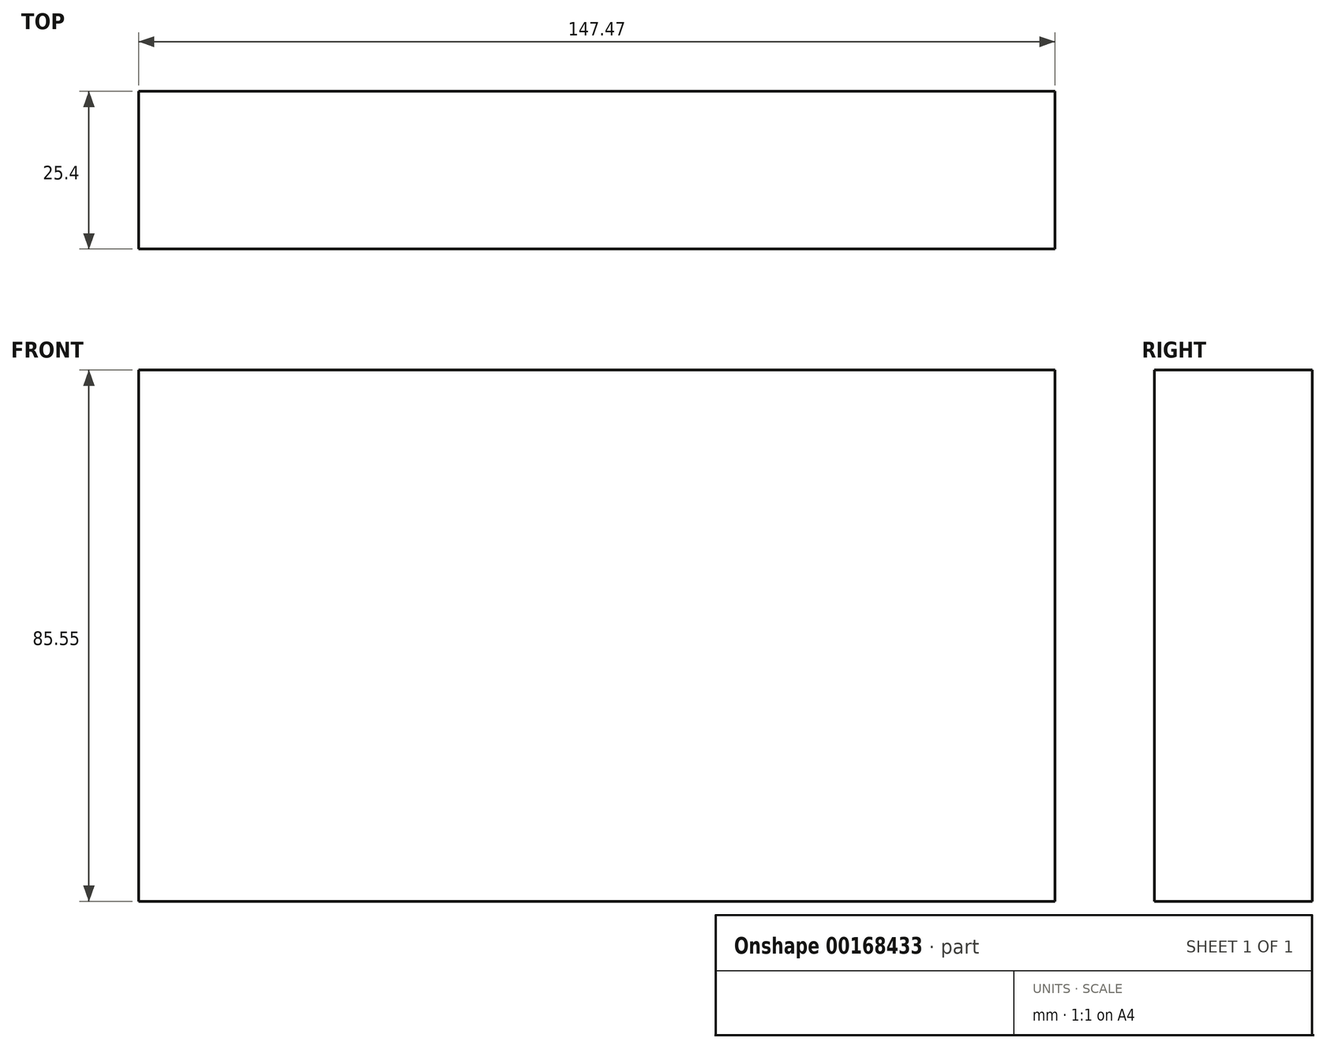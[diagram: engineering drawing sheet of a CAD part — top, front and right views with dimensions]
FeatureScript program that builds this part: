
annotation { "Feature Type Name" : "Feature", "Feature Type Description" : "" }
export const myFeature = defineFeature(function(context is Context, id is Id, definition is map)
    precondition{}
    {
        {
            var Q0;
            Q0=qCreatedBy(makeId("Front.planeOp"),FACE);
            var sketch = newSketch(context, id + "F0", { "sketchPlane" : qUnion([Q0])});
            skLineSegment(sketch, "E0.bottom", {"start": v(44.27, 43.86) * mm, "end": v(-103.2, 43.86) * mm});
            skLineSegment(sketch, "E0.top", {"start": v(44.27, 129.41) * mm, "end": v(-103.2, 129.41) * mm});
            skLineSegment(sketch, "E0.left", {"start": v(44.27, 43.86) * mm, "end": v(44.27, 129.41) * mm});
            skLineSegment(sketch, "E0.right", {"start": v(-103.2, 43.86) * mm, "end": v(-103.2, 129.41) * mm});
            skPoint(sketch, "E0.middle", {"position": v(-29.46, 86.64) * mm});
            skSolve(sketch);
        }
        {
            var Q0;
            Q0 = qSketchRegion(id + "F0", true);
            extrude(context, id + "F1", {"entities" : qUnion([Q0]), "depth" : 25.4 * mm});
        }
    });
